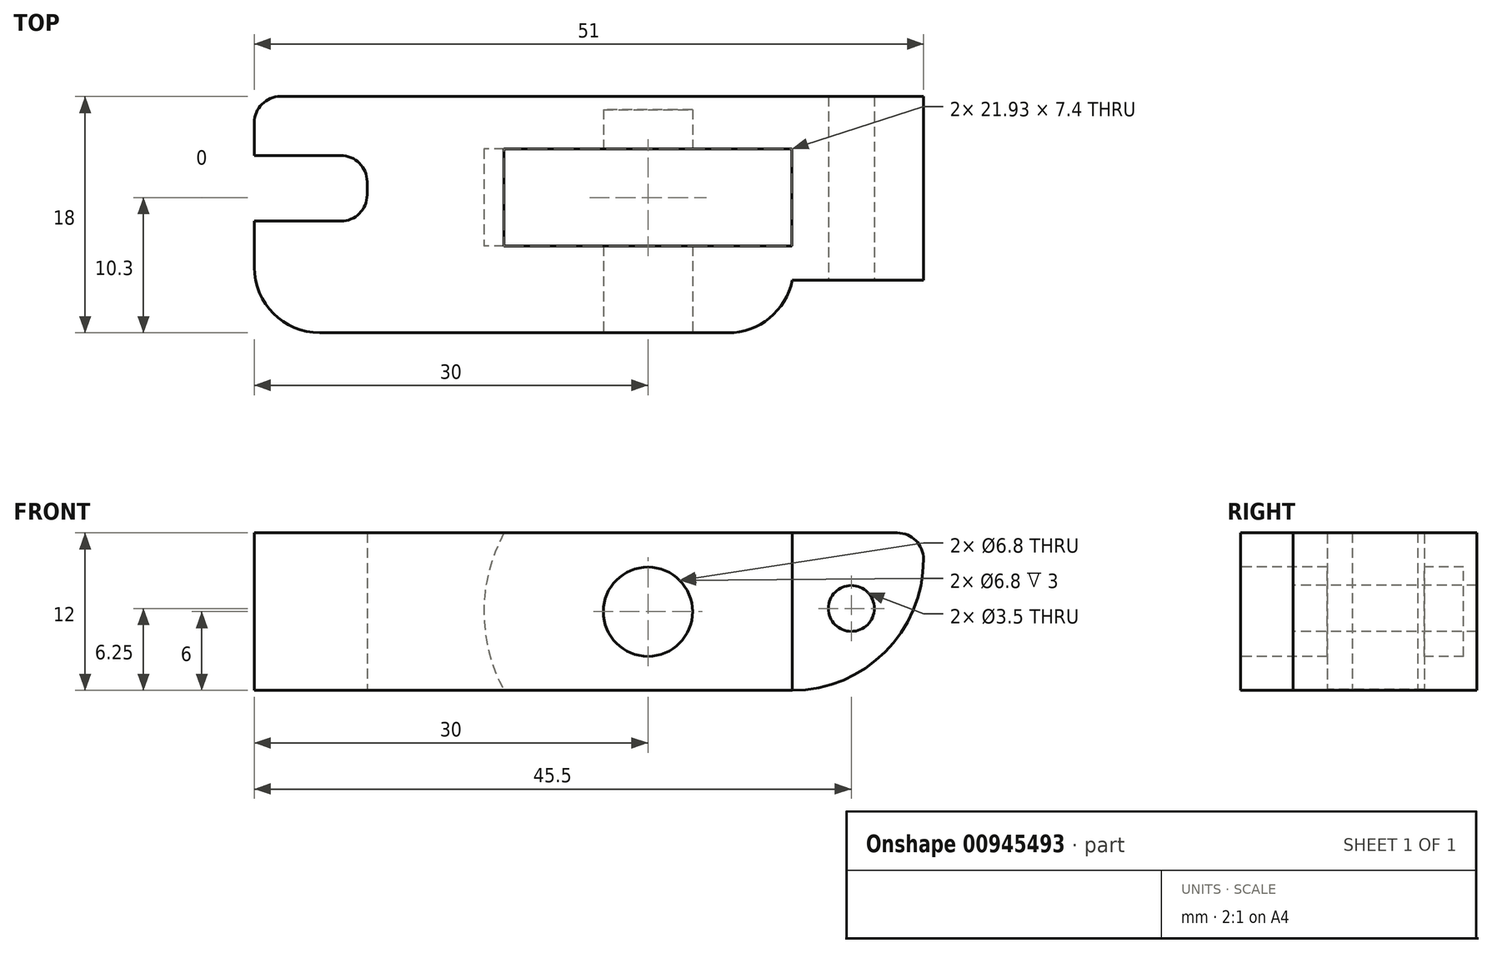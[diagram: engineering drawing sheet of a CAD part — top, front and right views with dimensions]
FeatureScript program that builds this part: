
annotation { "Feature Type Name" : "Feature", "Feature Type Description" : "" }
export const myFeature = defineFeature(function(context is Context, id is Id, definition is map)
    precondition{}
    {
        {
            var Q0;
            Q0=qCreatedBy(makeId("Top.planeOp"),FACE);
            var sketch = newSketch(context, id + "F0", { "sketchPlane" : qUnion([Q0])});
            skLineSegment(sketch, "E0.bottom", {"start": v(21, -4.5) * mm, "end": v(-30, -4.5) * mm});
            skLineSegment(sketch, "E0.top", {"start": v(21, 9.5) * mm, "end": v(-30, 9.5) * mm});
            skLineSegment(sketch, "E0.left", {"start": v(21, -4.5) * mm, "end": v(21, 9.5) * mm});
            skLineSegment(sketch, "E0.right", {"start": v(-30, -4.5) * mm, "end": v(-30, 9.5) * mm});
            skLineSegment(sketch, "E1.bottom", {"start": v(-30, -4.5) * mm, "end": v(11, -4.5) * mm});
            skLineSegment(sketch, "E1.top", {"start": v(-30, -8.5) * mm, "end": v(11, -8.5) * mm});
            skLineSegment(sketch, "E1.left", {"start": v(-30, -4.5) * mm, "end": v(-30, -8.5) * mm});
            skLineSegment(sketch, "E1.right", {"start": v(11, -4.5) * mm, "end": v(11, -8.5) * mm});
            skPoint(sketch, "E2.middle", {"position": v(0, 0) * mm});
            skLineSegment(sketch, "E3.bottom", {"start": v(-30, 0) * mm, "end": v(-21.4, 0) * mm});
            skLineSegment(sketch, "E3.top", {"start": v(-30, 5) * mm, "end": v(-21.4, 5) * mm});
            skLineSegment(sketch, "E3.left", {"start": v(-30, 0) * mm, "end": v(-30, 5) * mm});
            skLineSegment(sketch, "E3.right", {"start": v(-21.4, 0) * mm, "end": v(-21.4, 5) * mm});
            skPoint(sketch, "E4", {"position": v(-21.4, 2.5) * mm});
            skSolve(sketch);
        }
        {
            var Q0;
            {var subQ1=sQuery(id+"F0.wireOp",EDGE,"E0.top");Q0=makeQuery(id+"F0.imprint","IMPRINT",FACE,{"disambiguationData":[TD([[makeQuery(id+"F0.imprint","IMPRINT",EDGE,{"derivedFrom":subQ1}),1.0]])]});}
            var Q1;
            Q1=makeQuery(id+"F0.imprint","IMPRINT",FACE,{"disambiguationData":[TD([[makeQuery(id+"F0.imprint","IMPRINT",EDGE,{"derivedFrom":sQuery(id+"F0.wireOp",EDGE,"E1.top")}),1.0]])]});
            extrude(context, id + "F1", {"entities" : qUnion([Q0, Q1]), "endBound" : BoundingType.SYMMETRIC, "depth" : 12 * mm, "offsetDistance" : 25 * mm});
        }
        {
            var Q0;
            Q0=makeQuery(id+"F1.opExtrude","SWEPT_FACE",FACE,{"disambiguationData":[OSD([sQuery(id+"F0.wireOp",EDGE,"E1.top")])]});
            var sketch = newSketch(context, id + "F2", { "sketchPlane" : qUnion([Q0])});
            skCircle(sketch, "E5", {"center": v(0, 0) * mm, "radius": 3.4 * mm});
            skCircle(sketch, "E6", {"center": v(15.5, 0.25) * mm, "radius": 1.75 * mm});
            skCircle(sketch, "E7", {"center": v(0, 0) * mm, "radius": 12.5 * mm});
            skSolve(sketch);
        }
        {
            var Q0;
            Q0=makeQuery(id+"F2.imprint","IMPRINT",FACE,{"disambiguationData":[TD([[makeQuery(id+"F2.imprint","IMPRINT",EDGE,{"derivedFrom":sQuery(id+"F2.wireOp",EDGE,"E5")}),-1.0]])]});
            var Q1;
            {var subQ0=sQuery(id+"F2.wireOp",EDGE,"E7");var subQ1=makeQuery(id+"F1.opExtrude","SWEPT_EDGE",EDGE,{"disambiguationData":[OSD([sQuery(id+"F0.wireOp",EDGE,"E1.top"),sQuery(id+"F0.wireOp",EDGE,"E1.right")])]});var subQ2=makeQuery(id+"F2.imprint","INTERSECT",VERTEX,{"disambiguationData":[OD(0.0)],"derivedFrom":[subQ1,subQ0]});Q1=makeQuery(id+"F2.imprint","IMPRINT",FACE,{"disambiguationData":[TD([[makeQuery(id+"F2.imprint","IMPRINT",EDGE,{"disambiguationData":[TD([[subQ2,1.0]])],"derivedFrom":subQ0}),1.0]])]});}
            var Q2;
            Q2=makeQuery(id+"F2.imprint","IMPRINT",FACE,{"disambiguationData":[TD([[makeQuery(id+"F2.imprint","IMPRINT",EDGE,{"derivedFrom":sQuery(id+"F2.wireOp",EDGE,"E5")}),1.0]])]});
            extrude(context, id + "F3", {"entities" : qUnion([Q0, Q1, Q2]), "operationType" : NewBodyOperationType.REMOVE, "oppositeDirection" : true, "depth" : 14 * mm, "offsetDistance" : 25 * mm, "hasSecondDirection" : true, "secondDirectionOppositeDirection" : true, "secondDirectionDepth" : 6.6 * mm});
        }
        {
            var Q0;
            {var subQ0=sQuery(id+"F2.wireOp",EDGE,"E7");var subQ1=sQuery(id+"F0.wireOp",EDGE,"E1.top");Q0=makeQuery(id+"F3.boolean.opBoolean","COPY",EDGE,{"derivedFrom":makeQuery(id+"F3.opExtrude","SWEPT_EDGE",EDGE,{"disambiguationData":[OSD([subQ1,subQ0]),TDD([makeQuery(id+"F2.imprint","INTERSECT",VERTEX,{"disambiguationData":[OD(1.0)],"derivedFrom":[makeQuery(id+"F1.opExtrude","CAP_EDGE",EDGE,{"disambiguationData":[OSD([subQ1])],"isStart":false}),subQ0]})])]})});}
            var Q1;
            {var subQ0=sQuery(id+"F2.wireOp",EDGE,"E7");var subQ1=sQuery(id+"F0.wireOp",EDGE,"E1.top");Q1=makeQuery(id+"F3.boolean.opBoolean","COPY",EDGE,{"derivedFrom":makeQuery(id+"F3.opExtrude","SWEPT_EDGE",EDGE,{"disambiguationData":[OSD([subQ1,subQ0]),TDD([makeQuery(id+"F2.imprint","INTERSECT",VERTEX,{"disambiguationData":[OD(0.0)],"derivedFrom":[makeQuery(id+"F1.opExtrude","CAP_EDGE",EDGE,{"disambiguationData":[OSD([subQ1])],"isStart":false}),subQ0]})])]})});}
            var Q2;
            Q2=makeQuery(id+"F1.opExtrude","SWEPT_EDGE",EDGE,{"disambiguationData":[OSD([sQuery(id+"F0.wireOp",EDGE,"E1.top"),sQuery(id+"F0.wireOp",EDGE,"E1.left")])]});
            var Q3;
            Q3=makeQuery(id+"F1.opExtrude","SWEPT_EDGE",EDGE,{"disambiguationData":[OSD([sQuery(id+"F0.wireOp",EDGE,"E1.top"),sQuery(id+"F0.wireOp",EDGE,"E1.right")])]});
            fillet(context, id + "F4", {"entities" : qUnion([Q0, Q1, Q2, Q3]), "radius" : 5 * mm, "tangentPropagation" : true, "allowEdgeOverflow" : false});
        }
        {
            var Q0;
            Q0=makeQuery(id+"F2.imprint","IMPRINT",FACE,{"disambiguationData":[TD([[makeQuery(id+"F2.imprint","IMPRINT",EDGE,{"derivedFrom":sQuery(id+"F2.wireOp",EDGE,"E5")}),1.0]])]});
            var Q1;
            Q1=makeQuery(id+"F3.boolean.opBoolean","COPY",FACE,{"derivedFrom":makeQuery(id+"F3.opExtrude","CAP_FACE",FACE,{"disambiguationData":[OSD([sQuery(id+"F0.wireOp",EDGE,"E1.top"),sQuery(id+"F2.wireOp",EDGE,"E7")])],"isStart":false})});
            extrude(context, id + "F5", {"entities" : qUnion([Q0]), "operationType" : NewBodyOperationType.REMOVE, "endBound" : BoundingType.UP_TO_SURFACE, "oppositeDirection" : true, "depth" : 25 * mm, "endBoundEntityFace" : qUnion([Q1]), "hasOffset" : true, "offsetDistance" : -3 * mm});
        }
        {
            var Q0;
            Q0=makeQuery(id+"F1.opExtrude","CAP_EDGE",EDGE,{"disambiguationData":[OSD([sQuery(id+"F0.wireOp",EDGE,"E0.left")])],"isStart":true});
            fillet(context, id + "F6", {"entities" : qUnion([Q0]), "radius" : 10 * mm, "tangentPropagation" : true, "allowEdgeOverflow" : false});
        }
        {
            var Q0;
            Q0=makeQuery(id+"F1.opExtrude","CAP_EDGE",EDGE,{"disambiguationData":[OSD([sQuery(id+"F0.wireOp",EDGE,"E0.left")])],"isStart":false});
            fillet(context, id + "F7", {"entities" : qUnion([Q0]), "radius" : 2 * mm, "tangentPropagation" : true, "allowEdgeOverflow" : false});
        }
        {
            var Q0;
            Q0=makeQuery(id+"F1.opExtrude","SWEPT_EDGE",EDGE,{"disambiguationData":[OSD([sQuery(id+"F0.wireOp",EDGE,"E0.top"),sQuery(id+"F0.wireOp",EDGE,"E0.right")])]});
            var Q1;
            Q1=makeQuery(id+"F1.opExtrude","SWEPT_EDGE",EDGE,{"disambiguationData":[OSD([sQuery(id+"F0.wireOp",EDGE,"E3.top"),sQuery(id+"F0.wireOp",EDGE,"E3.right")])]});
            var Q2;
            Q2=makeQuery(id+"F1.opExtrude","SWEPT_EDGE",EDGE,{"disambiguationData":[OSD([sQuery(id+"F0.wireOp",EDGE,"E3.bottom"),sQuery(id+"F0.wireOp",EDGE,"E3.right")])]});
            fillet(context, id + "F8", {"entities" : qUnion([Q0, Q1, Q2]), "radius" : 2 * mm, "tangentPropagation" : true, "allowEdgeOverflow" : false});
        }
        {
            var Q0;
            Q0=makeQuery(id+"F2.imprint","IMPRINT",FACE,{"disambiguationData":[TD([[makeQuery(id+"F2.imprint","IMPRINT",EDGE,{"derivedFrom":sQuery(id+"F2.wireOp",EDGE,"E6")}),1.0]])]});
            extrude(context, id + "F9", {"entities" : qUnion([Q0]), "operationType" : NewBodyOperationType.REMOVE, "endBound" : BoundingType.THROUGH_ALL, "oppositeDirection" : true, "depth" : 25 * mm, "offsetDistance" : 25 * mm});
        }
    });
